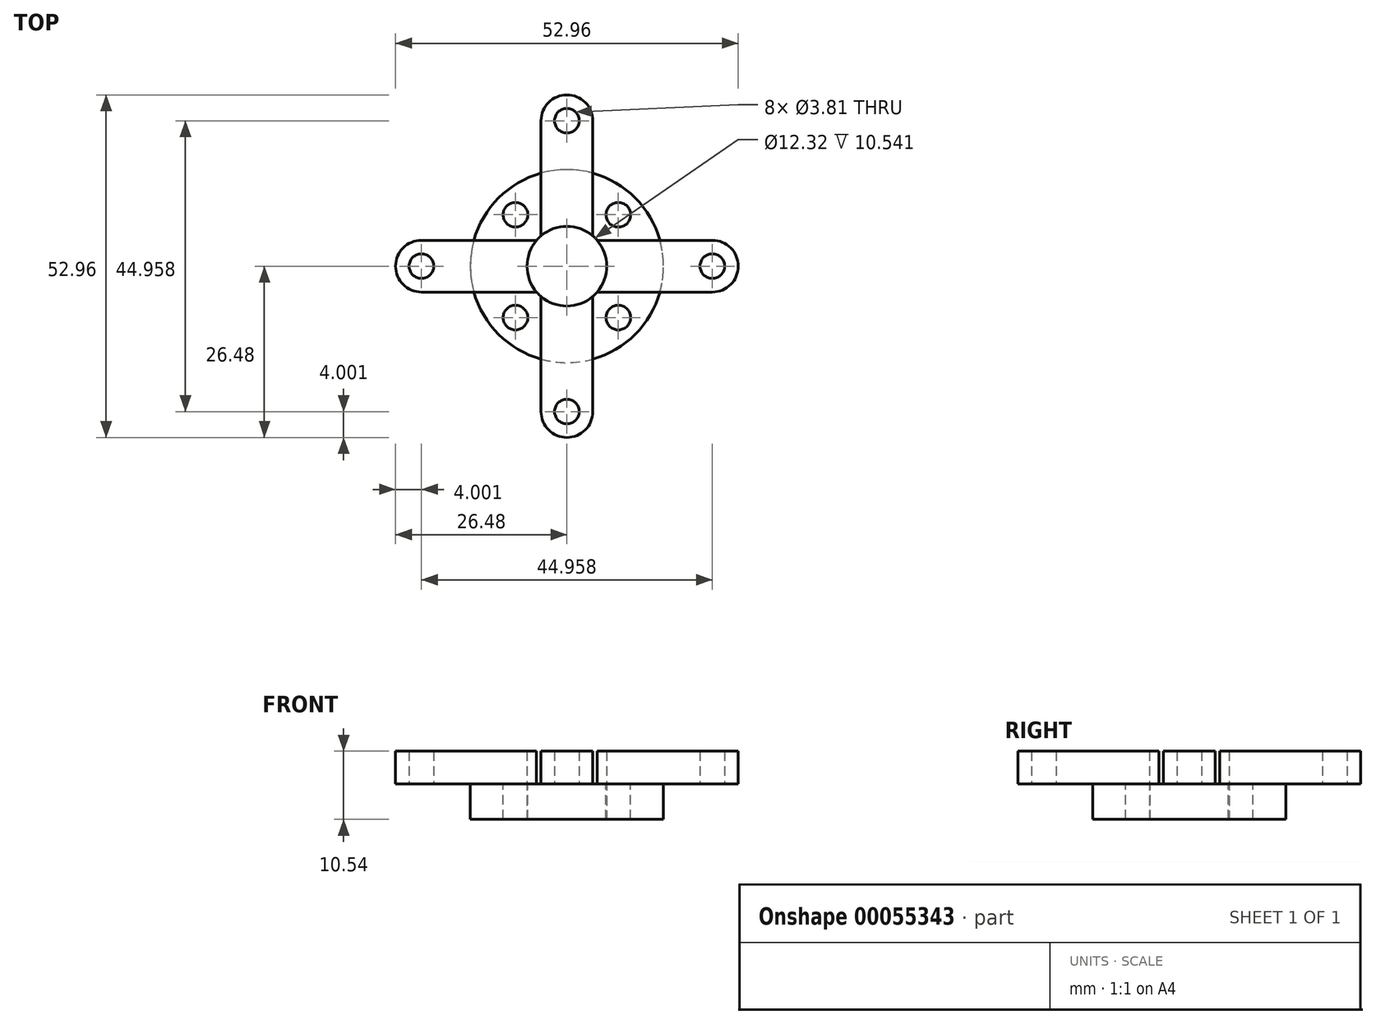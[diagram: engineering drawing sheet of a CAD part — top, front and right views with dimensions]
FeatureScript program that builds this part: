
annotation { "Feature Type Name" : "Feature", "Feature Type Description" : "" }
export const myFeature = defineFeature(function(context is Context, id is Id, definition is map)
    precondition{}
    {
        {
            var Q0;
            Q0=qCreatedBy(makeId("Top.planeOp"),FACE);
            var sketch = newSketch(context, id + "F0", { "sketchPlane" : qUnion([Q0])});
            skCircle(sketch, "E0", {"center": v(0, 0) * mm, "radius": 6.16 * mm});
            skCircle(sketch, "E1", {"center": v(0, 0) * mm, "radius": 14.92 * mm});
            skSolve(sketch);
        }
        {
            var Q0;
            Q0=makeQuery(id+"F0.imprint","IMPRINT",FACE,{"disambiguationData":[TD([[makeQuery(id+"F0.imprint","IMPRINT",EDGE,{"derivedFrom":sQuery(id+"F0.wireOp",EDGE,"E0")}),-1.0]])]});
            extrude(context, id + "F1", {"entities" : qUnion([Q0]), "depth" : 5.46 * mm});
        }
        {
            var Q0;
            Q0=makeQuery(id+"F1.opExtrude","CAP_FACE",FACE,{"disambiguationData":[OSD([sQuery(id+"F0.wireOp",EDGE,"E0"),sQuery(id+"F0.wireOp",EDGE,"E1")])],"isStart":false});
            var sketch = newSketch(context, id + "F2", { "sketchPlane" : qUnion([Q0])});
            skCircle(sketch, "E2", {"center": v(0, 11.24) * mm, "radius": 1.9 * mm});
            skCircle(sketch, "E3", {"center": v(0, 0) * mm, "radius": 4.46 * mm, "construction": true});
            skCircle(sketch, "E4.1.0", {"center": v(-11.24, 0) * mm, "radius": 1.9 * mm});
            skCircle(sketch, "E4.2.0", {"center": v(0, -11.24) * mm, "radius": 1.9 * mm});
            skCircle(sketch, "E4.3.0", {"center": v(11.24, 0) * mm, "radius": 1.9 * mm});
            skLineSegment(sketch, "E5", {"start": v(0, 0) * mm, "end": v(0, 0) * mm});
            skSolve(sketch);
        }
        {
            var Q0;
            Q0=makeQuery(id+"F2.imprint","IMPRINT",FACE,{"disambiguationData":[TD([[makeQuery(id+"F2.imprint","IMPRINT",EDGE,{"derivedFrom":sQuery(id+"F2.wireOp",EDGE,"E4.1.0")}),1.0]])]});
            var Q1;
            Q1=makeQuery(id+"F2.imprint","IMPRINT",FACE,{"disambiguationData":[TD([[makeQuery(id+"F2.imprint","IMPRINT",EDGE,{"derivedFrom":sQuery(id+"F2.wireOp",EDGE,"E2")}),1.0]])]});
            var Q2;
            Q2=makeQuery(id+"F2.imprint","IMPRINT",FACE,{"disambiguationData":[TD([[makeQuery(id+"F2.imprint","IMPRINT",EDGE,{"derivedFrom":sQuery(id+"F2.wireOp",EDGE,"E4.3.0")}),1.0]])]});
            var Q3;
            Q3=makeQuery(id+"F2.imprint","IMPRINT",FACE,{"disambiguationData":[TD([[makeQuery(id+"F2.imprint","IMPRINT",EDGE,{"derivedFrom":sQuery(id+"F2.wireOp",EDGE,"E4.2.0")}),1.0]])]});
            extrude(context, id + "F3", {"entities" : qUnion([Q0, Q1, Q2, Q3]), "operationType" : NewBodyOperationType.REMOVE, "oppositeDirection" : true, "depth" : 25.4 * mm});
        }
        {
            var Q0;
            Q0=qCreatedBy(makeId("Right.planeOp"),FACE);
            var sketch = newSketch(context, id + "F4", { "sketchPlane" : qUnion([Q0])});
            skLineSegment(sketch, "E6", {"start": v(0, 0) * mm, "end": v(0, 19.9) * mm, "construction": true});
            skSolve(sketch);
        }
        {
            var Q0;
            Q0=makeQuery(id+"F1.opExtrude","SWEPT_BODY",BODY,{"disambiguationData":[OSD([sQuery(id+"F0.wireOp",EDGE,"E0"),sQuery(id+"F0.wireOp",EDGE,"E1")])]});
            var Q1;
            Q1=sQuery(id+"F4.wireOp",EDGE,"E6");
            transform(context, id + "F5", {"entities" : qUnion([Q0]), "transformType" : TransformType.ROTATION, "transformAxis" : qUnion([Q1]), "angle" : 45 * degree, "makeCopy" : false});
        }
        {
            var Q0;
            Q0=makeQuery(id+"F1.opExtrude","CAP_FACE",FACE,{"disambiguationData":[OSD([sQuery(id+"F0.wireOp",EDGE,"E0"),sQuery(id+"F0.wireOp",EDGE,"E1")])],"isStart":false});
            var sketch = newSketch(context, id + "F6", { "sketchPlane" : qUnion([Q0])});
            skLineSegment(sketch, "E7", {"start": v(0, 6.16) * mm, "end": v(0, 26.48) * mm, "construction": true});
            skArc(sketch, "E8", {"start": v(4, 22.48) * mm, "mid": v(0, 26.48) * mm, "end": v(-4, 22.48) * mm});
            skLineSegment(sketch, "E9", {"start": v(-4, 22.48) * mm, "end": v(-4, 4.68) * mm});
            skCircle(sketch, "E10", {"center": v(0, 22.48) * mm, "radius": 1.9 * mm});
            skLineSegment(sketch, "E11.1.0", {"start": v(-22.48, 4) * mm, "end": v(-4.68, 4) * mm});
            skLineSegment(sketch, "E11.1.1", {"start": v(-22.48, -4) * mm, "end": v(-4.68, -4) * mm});
            skCircle(sketch, "E11.1.2", {"center": v(-22.48, 0) * mm, "radius": 1.9 * mm});
            skArc(sketch, "E11.1.3", {"start": v(-22.48, 4) * mm, "mid": v(-26.48, 0) * mm, "end": v(-22.48, -4) * mm});
            skLineSegment(sketch, "E11.2.0", {"start": v(-4, -22.48) * mm, "end": v(-4, -4.68) * mm});
            skLineSegment(sketch, "E11.2.1", {"start": v(4, -22.48) * mm, "end": v(4, -4.68) * mm});
            skCircle(sketch, "E11.2.2", {"center": v(0, -22.48) * mm, "radius": 1.9 * mm});
            skArc(sketch, "E11.2.3", {"start": v(-4, -22.48) * mm, "mid": v(0, -26.48) * mm, "end": v(4, -22.48) * mm});
            skPoint(sketch, "E11.center", {"position": v(0, 0) * mm});
            skLineSegment(sketch, "E12.2.3.0", {"start": v(22.48, -4) * mm, "end": v(4.68, -4) * mm});
            skLineSegment(sketch, "E12.3.3.0", {"start": v(22.48, 4) * mm, "end": v(4.68, 4) * mm});
            skCircle(sketch, "E12.6.3.0", {"center": v(22.48, 0) * mm, "radius": 1.9 * mm});
            skArc(sketch, "E12.8.3.0", {"start": v(22.48, -4) * mm, "mid": v(26.48, 0) * mm, "end": v(22.48, 4) * mm});
            skLineSegment(sketch, "E13", {"start": v(4, 22.48) * mm, "end": v(4, 4.68) * mm});
            skSolve(sketch);
        }
        {
            var Q0;
            Q0=makeQuery(id+"F6.imprint","IMPRINT",FACE,{"disambiguationData":[TD([[makeQuery(id+"F6.imprint","IMPRINT",EDGE,{"derivedFrom":sQuery(id+"F6.wireOp",EDGE,"E11.1.2")}),-1.0]])]});
            var Q1;
            {var subQ0=sQuery(id+"F6.wireOp",EDGE,"E11.1.0");var subQ1=makeQuery(id+"F1.opExtrude","CAP_EDGE",EDGE,{"disambiguationData":[OSD([sQuery(id+"F0.wireOp",EDGE,"E0")])],"isStart":false});var subQ2=makeQuery(id+"F6.imprint","INTERSECT",VERTEX,{"derivedFrom":[subQ1,subQ0]});Q1=makeQuery(id+"F6.imprint","IMPRINT",FACE,{"disambiguationData":[TD([[makeQuery(id+"F6.imprint","IMPRINT",EDGE,{"disambiguationData":[TD([[subQ2,1.0]])],"derivedFrom":subQ0}),-1.0]])]});}
            var Q2;
            {var subQ0=sQuery(id+"F6.wireOp",EDGE,"E12.2.3.0");var subQ1=makeQuery(id+"F1.opExtrude","CAP_EDGE",EDGE,{"disambiguationData":[OSD([sQuery(id+"F0.wireOp",EDGE,"E0")])],"isStart":false});var subQ2=makeQuery(id+"F6.imprint","INTERSECT",VERTEX,{"derivedFrom":[subQ1,subQ0]});Q2=makeQuery(id+"F6.imprint","IMPRINT",FACE,{"disambiguationData":[TD([[makeQuery(id+"F6.imprint","IMPRINT",EDGE,{"disambiguationData":[TD([[subQ2,1.0]])],"derivedFrom":subQ0}),-1.0]])]});}
            var Q3;
            Q3=makeQuery(id+"F6.imprint","IMPRINT",FACE,{"disambiguationData":[TD([[makeQuery(id+"F6.imprint","IMPRINT",EDGE,{"derivedFrom":sQuery(id+"F6.wireOp",EDGE,"E12.6.3.0")}),-1.0]])]});
            var Q4;
            {var subQ1=sQuery(id+"F6.wireOp",EDGE,"E8");Q4=makeQuery(id+"F6.imprint","IMPRINT",FACE,{"disambiguationData":[TD([[makeQuery(id+"F6.imprint","IMPRINT",EDGE,{"derivedFrom":subQ1}),1.0]])]});}
            var Q5;
            {var subQ0=sQuery(id+"F6.wireOp",EDGE,"E9");var subQ1=makeQuery(id+"F1.opExtrude","CAP_EDGE",EDGE,{"disambiguationData":[OSD([sQuery(id+"F0.wireOp",EDGE,"E0")])],"isStart":false});var subQ2=makeQuery(id+"F6.imprint","INTERSECT",VERTEX,{"derivedFrom":[subQ1,subQ0]});Q5=makeQuery(id+"F6.imprint","IMPRINT",FACE,{"disambiguationData":[TD([[makeQuery(id+"F6.imprint","IMPRINT",EDGE,{"disambiguationData":[TD([[subQ2,1.0]])],"derivedFrom":subQ0}),1.0]])]});}
            var Q6;
            Q6=makeQuery(id+"F6.imprint","IMPRINT",FACE,{"disambiguationData":[TD([[makeQuery(id+"F6.imprint","IMPRINT",EDGE,{"derivedFrom":sQuery(id+"F6.wireOp",EDGE,"E11.2.2")}),-1.0]])]});
            var Q7;
            {var subQ0=sQuery(id+"F6.wireOp",EDGE,"E11.2.0");var subQ1=makeQuery(id+"F1.opExtrude","CAP_EDGE",EDGE,{"disambiguationData":[OSD([sQuery(id+"F0.wireOp",EDGE,"E0")])],"isStart":false});var subQ2=makeQuery(id+"F6.imprint","INTERSECT",VERTEX,{"derivedFrom":[subQ1,subQ0]});Q7=makeQuery(id+"F6.imprint","IMPRINT",FACE,{"disambiguationData":[TD([[makeQuery(id+"F6.imprint","IMPRINT",EDGE,{"disambiguationData":[TD([[subQ2,1.0]])],"derivedFrom":subQ0}),-1.0]])]});}
            extrude(context, id + "F7", {"entities" : qUnion([Q0, Q1, Q2, Q3, Q4, Q5, Q6, Q7]), "operationType" : NewBodyOperationType.ADD, "depth" : 5.08 * mm});
        }
    });
